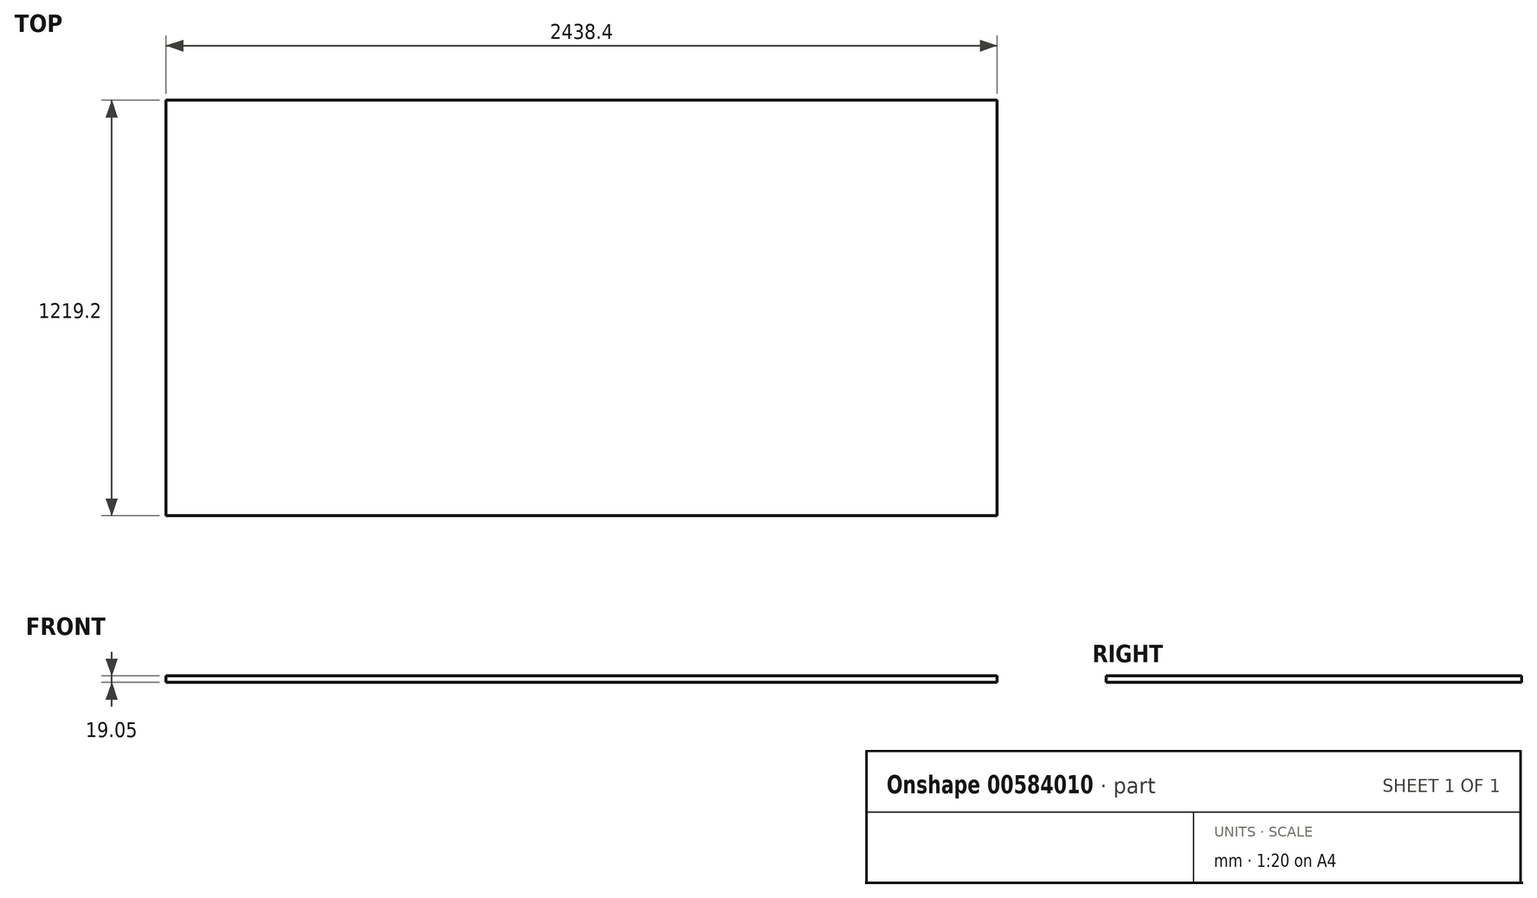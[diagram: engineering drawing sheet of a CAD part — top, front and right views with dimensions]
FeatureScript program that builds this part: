
annotation { "Feature Type Name" : "Feature", "Feature Type Description" : "" }
export const myFeature = defineFeature(function(context is Context, id is Id, definition is map)
    precondition{}
    {
        {
            var Q0;
            Q0=qCreatedBy(makeId("Top.planeOp"),FACE);
            var sketch = newSketch(context, id + "F0", { "sketchPlane" : qUnion([Q0])});
            skLineSegment(sketch, "E0.bottom", {"start": v(-1221.57, -709.24) * mm, "end": v(1216.83, -709.24) * mm});
            skLineSegment(sketch, "E0.top", {"start": v(-1221.57, 509.96) * mm, "end": v(1216.83, 509.96) * mm});
            skLineSegment(sketch, "E0.left", {"start": v(-1221.57, -709.24) * mm, "end": v(-1221.57, 509.96) * mm});
            skLineSegment(sketch, "E0.right", {"start": v(1216.83, -709.24) * mm, "end": v(1216.83, 509.96) * mm});
            skSolve(sketch);
        }
        {
            var Q0;
            Q0=makeQuery(id+"F0.imprint","IMPRINT",FACE,{"disambiguationData":[TD([[makeQuery(id+"F0.imprint","IMPRINT",EDGE,{"derivedFrom":sQuery(id+"F0.wireOp",EDGE,"E0.bottom")}),1.0]])]});
            extrude(context, id + "F1", {"entities" : qUnion([Q0]), "depth" : 19.05 * mm, "offsetDistance" : 25.4 * mm});
        }
    });
